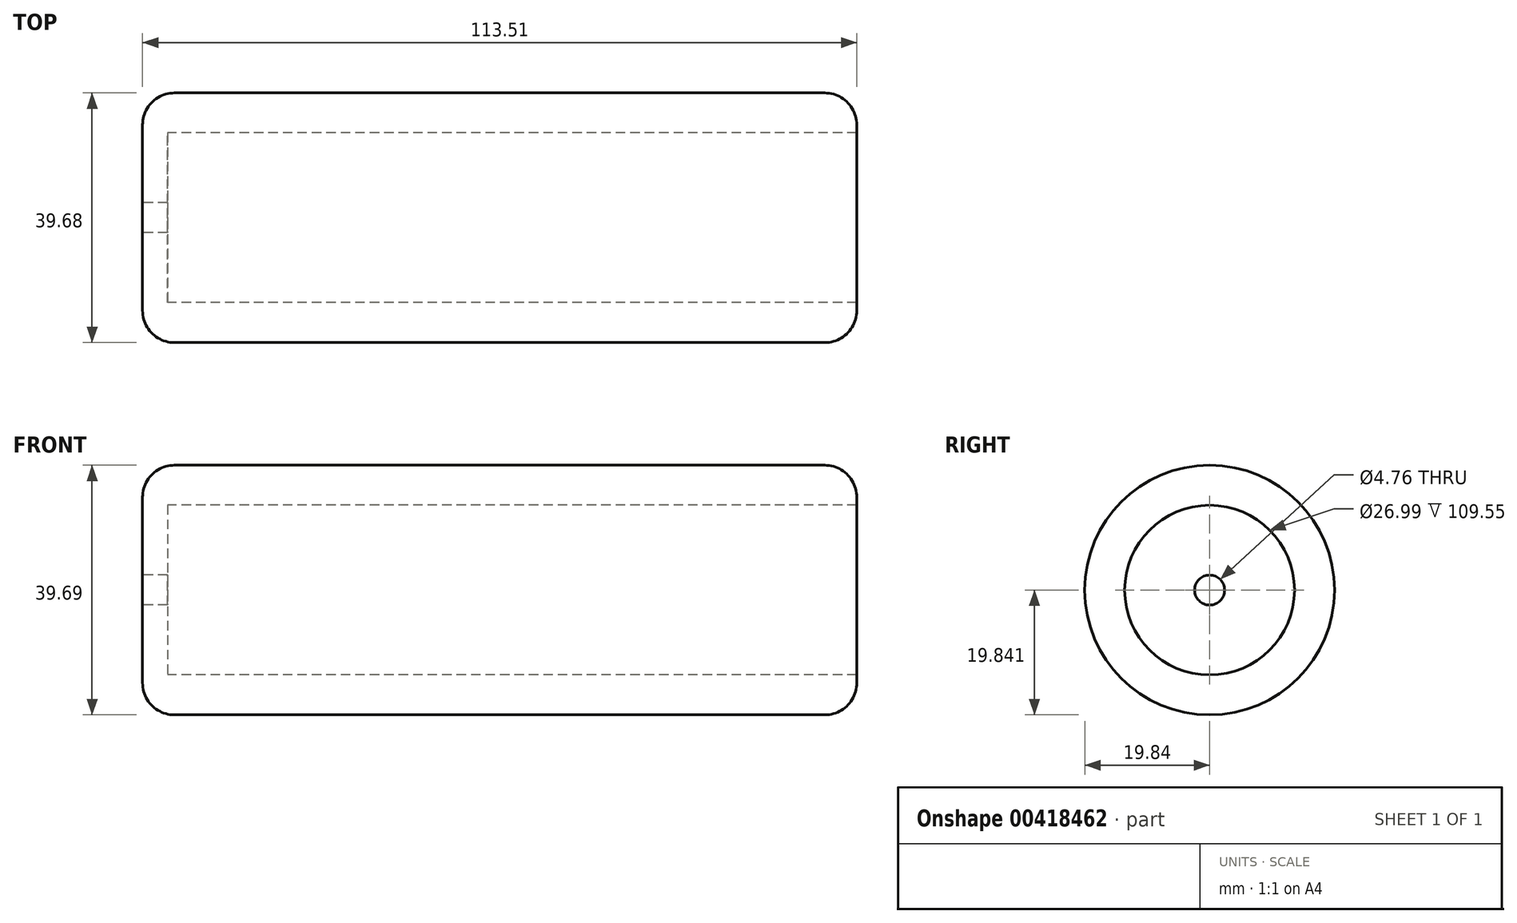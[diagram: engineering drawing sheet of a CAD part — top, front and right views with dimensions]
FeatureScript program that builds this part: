
annotation { "Feature Type Name" : "Feature", "Feature Type Description" : "" }
export const myFeature = defineFeature(function(context is Context, id is Id, definition is map)
    precondition{}
    {
        {
            var Q0;
            Q0=qCreatedBy(makeId("Front.planeOp"),FACE);
            var sketch = newSketch(context, id + "F0", { "sketchPlane" : qUnion([Q0])});
            skLineSegment(sketch, "E0", {"start": v(-19.31, 0) * mm, "end": v(-15.35, 0) * mm});
            skLineSegment(sketch, "E1", {"start": v(-19.31, 2.38) * mm, "end": v(107.69, 2.38) * mm, "construction": true});
            skLineSegment(sketch, "E2", {"start": v(-19.31, 0) * mm, "end": v(-19.31, -17.46) * mm});
            skLineSegment(sketch, "E3", {"start": v(-19.31, -17.46) * mm, "end": v(94.2, -17.46) * mm});
            skLineSegment(sketch, "E4", {"start": v(94.2, -17.46) * mm, "end": v(94.2, -11.11) * mm});
            skLineSegment(sketch, "E5", {"start": v(-15.35, 0) * mm, "end": v(-15.35, -11.11) * mm});
            skLineSegment(sketch, "E6", {"start": v(-15.35, -11.11) * mm, "end": v(94.2, -11.11) * mm});
            skSolve(sketch);
        }
        {
            var Q0;
            Q0 = qSketchRegion(id + "F0", true);
            var Q1;
            Q1=sQuery(id+"F0.wireOp",EDGE,"E1");
            revolve(context, id + "F1", {"entities" : qUnion([Q0]), "axis" : qUnion([Q1]), "revolveType" : RevolveType.FULL});
        }
        {
            var Q0;
            Q0=makeQuery(id+"F1.opRevolve","SWEPT_EDGE",EDGE,{"disambiguationData":[OSD([sQuery(id+"F0.wireOp",EDGE,"E2"),sQuery(id+"F0.wireOp",EDGE,"E3")])]});
            var Q1;
            Q1=makeQuery(id+"F1.opRevolve","SWEPT_FACE",FACE,{"disambiguationData":[OSD([sQuery(id+"F0.wireOp",EDGE,"E3")])]});
            fillet(context, id + "F2", {"entities" : qUnion([Q0, Q1]), "radius" : 5.08 * mm, "tangentPropagation" : true, "allowEdgeOverflow" : false});
        }
    });
